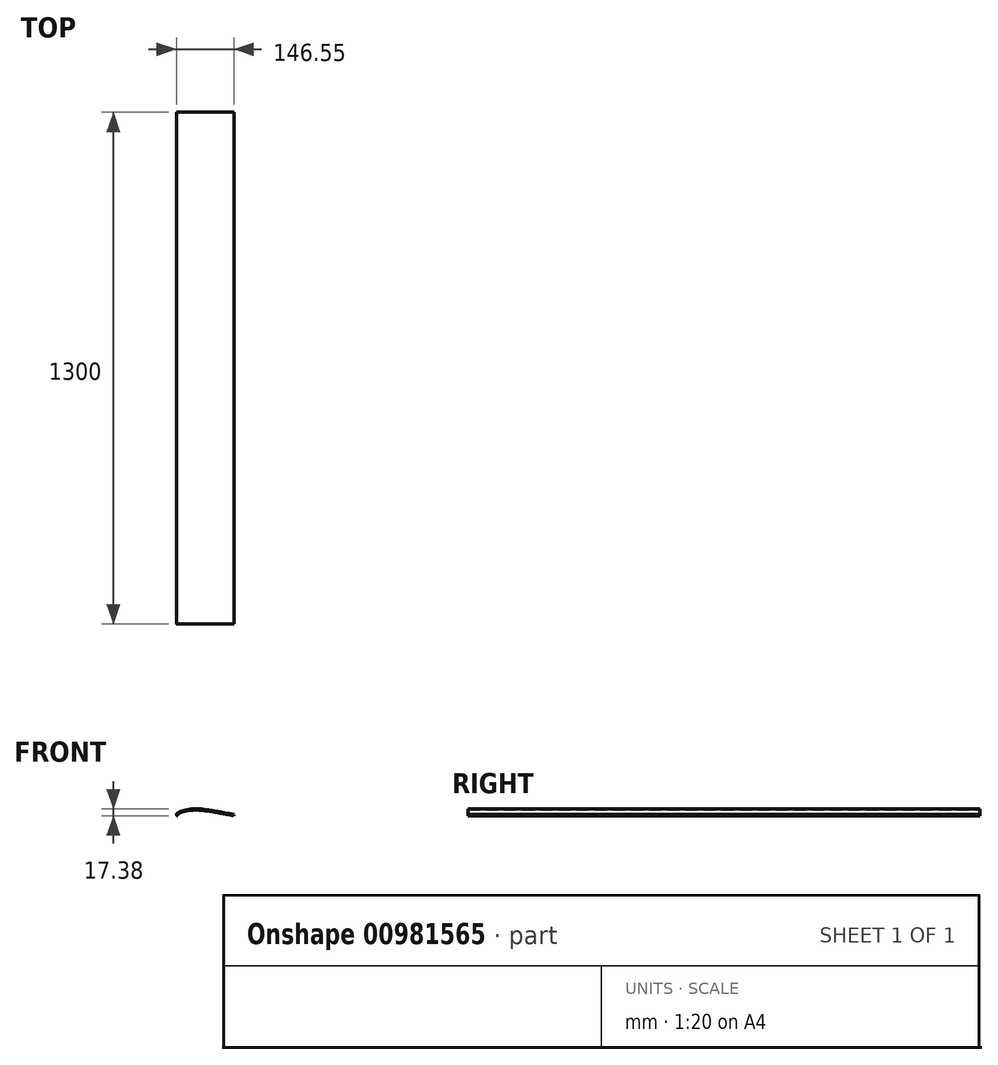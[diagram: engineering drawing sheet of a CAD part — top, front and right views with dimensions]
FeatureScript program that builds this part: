
annotation { "Feature Type Name" : "Feature", "Feature Type Description" : "" }
export const myFeature = defineFeature(function(context is Context, id is Id, definition is map)
    precondition{}
    {
        {
            var Q0;
            Q0=qCreatedBy(makeId("Front.planeOp"),FACE);
            var sketch = newSketch(context, id + "F0", { "sketchPlane" : qUnion([Q0])});
            skLineSegment(sketch, "E0", {"start": v(0, 0) * mm, "end": v(102, 0) * mm});
            skLineSegment(sketch, "E1.bottom", {"start": v(26, 0) * mm, "end": v(69, 0) * mm});
            skLineSegment(sketch, "E1.top", {"start": v(26, 10) * mm, "end": v(69, 10) * mm, "construction": true});
            skLineSegment(sketch, "E1.left", {"start": v(26, 0) * mm, "end": v(26, 10) * mm, "construction": true});
            skLineSegment(sketch, "E1.right", {"start": v(69, 0) * mm, "end": v(69, 10) * mm, "construction": true});
            skLineSegment(sketch, "E2", {"start": v(102, 0) * mm, "end": v(127, 0) * mm});
            skLineSegment(sketch, "E3.bottom", {"start": v(9, 0) * mm, "end": v(26, 0) * mm});
            skLineSegment(sketch, "E3.top", {"start": v(9, 5) * mm, "end": v(26, 5) * mm, "construction": true});
            skLineSegment(sketch, "E3.left", {"start": v(9, 0) * mm, "end": v(9, 5) * mm, "construction": true});
            skLineSegment(sketch, "E3.right", {"start": v(26, 0) * mm, "end": v(26, 5) * mm});
            skFitSpline(sketch, "E4", {"points": [v(0, 0) * mm, v(9, 5) * mm, v(26, 10) * mm, v(69, 10) * mm, v(127, 0) * mm], "startDerivative": vector(100.72, 59.29) * mm, "endDerivative": vector(193.95, -38.05) * mm});
            skLineSegment(sketch, "E5", {"start": v(0, 0) * mm, "end": v(0, -3) * mm});
            skLineSegment(sketch, "E6", {"start": v(0, -3) * mm, "end": v(143, -3) * mm});
            skLineSegment(sketch, "E7", {"start": v(143, -3) * mm, "end": v(127, 0) * mm});
            skLineSegment(sketch, "E8", {"start": v(143, -3) * mm, "end": v(143.55, -0.05) * mm});
            skFitSpline(sketch, "E9", {"points": [v(143.55, -0.05) * mm, v(69.31, 12.98) * mm, v(25.51, 12.96) * mm, v(7.77, 7.74) * mm, v(-1.5, 2.6) * mm], "startDerivative": vector(-307.51, 59.8) * mm, "endDerivative": vector(-155.36, -89.7) * mm});
            skArc(sketch, "E10", {"start": v(-1.5, 2.6) * mm, "mid": v(-2.9, -0.78) * mm, "end": v(0, -3) * mm});
            skLineSegment(sketch, "E11", {"start": v(26, 10) * mm, "end": v(44.77, 13.08) * mm, "construction": true});
            skLineSegment(sketch, "E12", {"start": v(26, 10) * mm, "end": v(25.51, 12.96) * mm, "construction": true});
            skLineSegment(sketch, "E13", {"start": v(9, 5) * mm, "end": v(29.33, 14.1) * mm, "construction": true});
            skLineSegment(sketch, "E14", {"start": v(9, 5) * mm, "end": v(7.77, 7.74) * mm, "construction": true});
            skLineSegment(sketch, "E15", {"start": v(69, 10) * mm, "end": v(167.4, -0.31) * mm, "construction": true});
            skLineSegment(sketch, "E16", {"start": v(69, 10) * mm, "end": v(69.31, 12.98) * mm, "construction": true});
            skLineSegment(sketch, "E17", {"start": v(47.5, 10) * mm, "end": v(47.5, -11.43) * mm, "construction": true});
            skLineSegment(sketch, "E18", {"start": v(47.5, -11.43) * mm, "end": v(-3, -11.43) * mm, "construction": true});
            skLineSegment(sketch, "E19", {"start": v(-3, -11.43) * mm, "end": v(-3, 0) * mm, "construction": true});
            skLineSegment(sketch, "E20", {"start": v(31, 10) * mm, "end": v(31, 0) * mm, "construction": true});
            skLineSegment(sketch, "E21", {"start": v(64, 10) * mm, "end": v(64, 0) * mm, "construction": true});
            skLineSegment(sketch, "E22", {"start": v(-1.5, 2.6) * mm, "end": v(0, 0) * mm, "construction": true});
            skLineSegment(sketch, "E23", {"start": v(0, 0) * mm, "end": v(-2.9, -0.78) * mm, "construction": true});
            skArc(sketch, "E24", {"start": v(-2.9, -0.78) * mm, "mid": v(-1.83, -2.38) * mm, "end": v(0, -3) * mm});
            skCircle(sketch, "E25", {"center": v(60, 4) * mm, "radius": 4 * mm});
            skLineSegment(sketch, "E26", {"start": v(64, 8) * mm, "end": v(56, 8) * mm});
            skLineSegment(sketch, "E27", {"start": v(56, 8) * mm, "end": v(56, 0) * mm});
            skLineSegment(sketch, "E28", {"start": v(56, 8) * mm, "end": v(56, 11.03) * mm});
            skLineSegment(sketch, "E29", {"start": v(56, 11.03) * mm, "end": v(64, 10) * mm});
            skLineSegment(sketch, "E30", {"start": v(51, 0) * mm, "end": v(51, 11.03) * mm});
            skLineSegment(sketch, "E31", {"start": v(51, 11.03) * mm, "end": v(56, 11.03) * mm});
            skSolve(sketch);
        }
        {
            var Q0;
            Q0=makeQuery(id+"F0.imprint","IMPRINT",FACE,{"disambiguationData":[TD([[makeQuery(id+"F0.imprint","IMPRINT",EDGE,{"derivedFrom":sQuery(id+"F0.wireOp",EDGE,"E4")}),1.0]])]});
            var Q1;
            {var subQ1=sQuery(id+"F0.wireOp",EDGE,"E1.bottom");Q1=makeQuery(id+"F0.imprint","IMPRINT",FACE,{"disambiguationData":[TD([[makeQuery(id+"F0.imprint","IMPRINT",EDGE,{"derivedFrom":subQ1}),-1.0]])]});}
            extrude(context, id + "F1", {"entities" : qUnion([Q0, Q1]), "endBound" : BoundingType.SYMMETRIC, "depth" : 1300 * mm, "offsetDistance" : 25 * mm});
        }
    });
